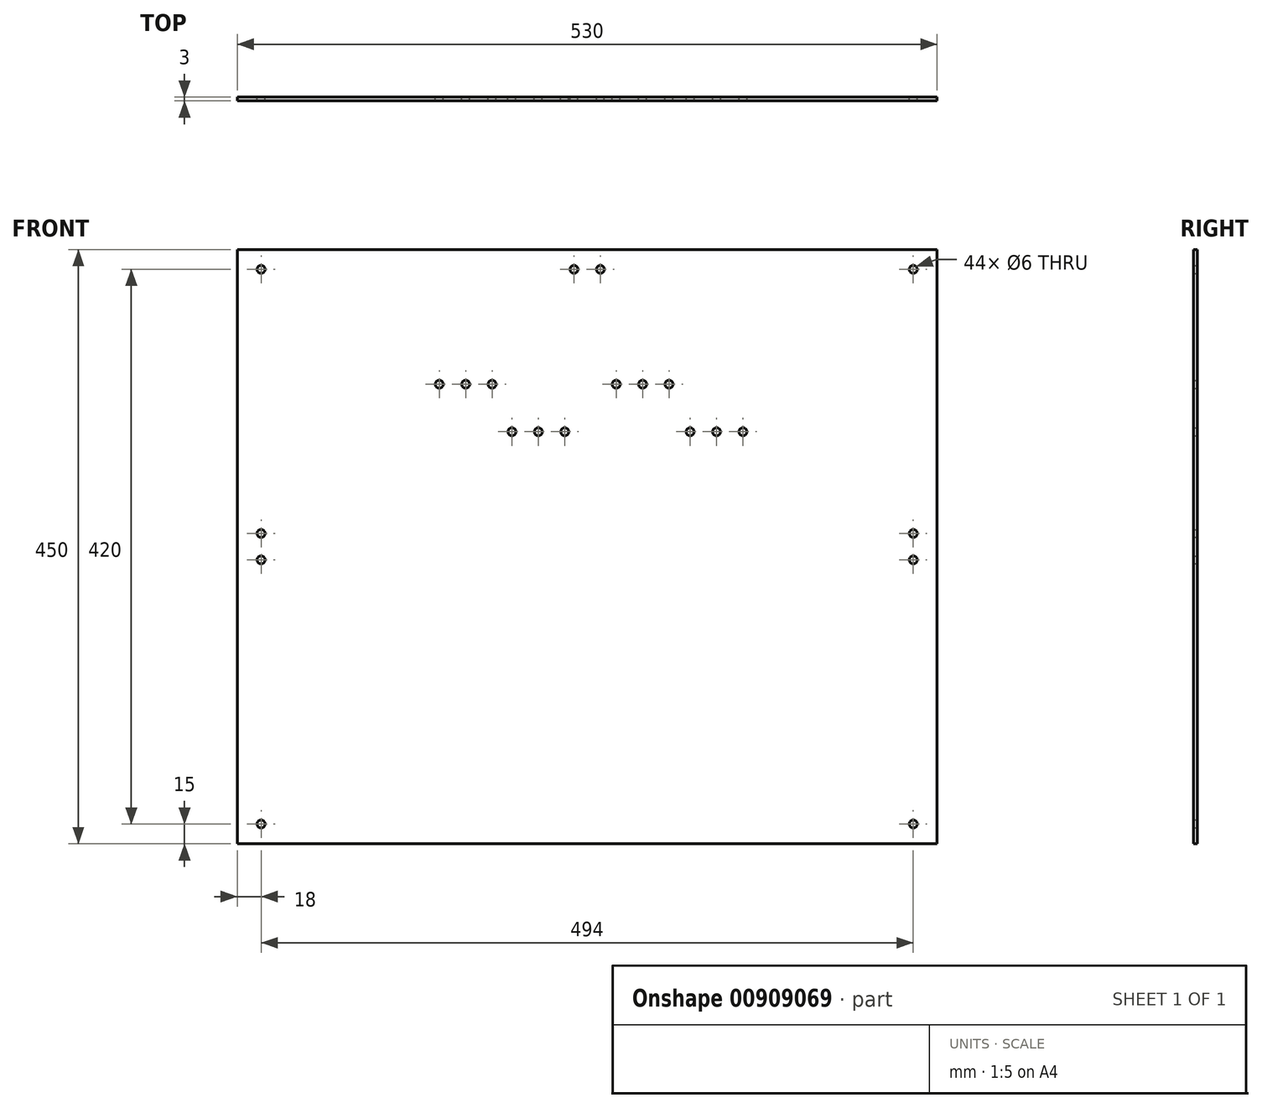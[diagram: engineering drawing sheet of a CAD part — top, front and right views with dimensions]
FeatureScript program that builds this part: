
annotation { "Feature Type Name" : "Feature", "Feature Type Description" : "" }
export const myFeature = defineFeature(function(context is Context, id is Id, definition is map)
    precondition{}
    {
        {
            var Q0;
            Q0=qCreatedBy(makeId("Front.planeOp"),FACE);
            var sketch = newSketch(context, id + "F0", { "sketchPlane" : qUnion([Q0])});
            skLineSegment(sketch, "E0.bottom", {"start": v(0, 0) * mm, "end": v(530, 0) * mm});
            skLineSegment(sketch, "E0.top", {"start": v(0, 450) * mm, "end": v(530, 450) * mm});
            skLineSegment(sketch, "E0.left", {"start": v(0, 0) * mm, "end": v(0, 450) * mm});
            skLineSegment(sketch, "E0.right", {"start": v(530, 0) * mm, "end": v(530, 450) * mm});
            skCircle(sketch, "E1", {"center": v(18, 15) * mm, "radius": 3 * mm});
            skCircle(sketch, "E2", {"center": v(512, 15) * mm, "radius": 3 * mm});
            skCircle(sketch, "E3", {"center": v(18, 435) * mm, "radius": 3 * mm});
            skCircle(sketch, "E4", {"center": v(512, 435) * mm, "radius": 3 * mm});
            skLineSegment(sketch, "E5.bottom", {"start": v(395, 80) * mm, "end": v(135, 80) * mm});
            skLineSegment(sketch, "E5.top", {"start": v(395, 330) * mm, "end": v(135, 330) * mm});
            skLineSegment(sketch, "E5.left", {"start": v(410, 95) * mm, "end": v(410, 315) * mm});
            skLineSegment(sketch, "E5.right", {"start": v(120, 95) * mm, "end": v(120, 315) * mm});
            skPoint(sketch, "E5.middle", {"position": v(265, 205) * mm});
            skPoint(sketch, "E6.visualSharp", {"position": v(120, 330) * mm});
            skArc(sketch, "E6.filletArc", {"start": v(135, 330) * mm, "mid": v(124.4, 325.6) * mm, "end": v(120, 315) * mm});
            skPoint(sketch, "E7.visualSharp", {"position": v(410, 330) * mm});
            skArc(sketch, "E7.filletArc", {"start": v(410, 315) * mm, "mid": v(405.6, 325.6) * mm, "end": v(395, 330) * mm});
            skPoint(sketch, "E8.visualSharp", {"position": v(120, 80) * mm});
            skArc(sketch, "E8.filletArc", {"start": v(120, 95) * mm, "mid": v(124.4, 84.4) * mm, "end": v(135, 80) * mm});
            skPoint(sketch, "E9.visualSharp", {"position": v(410, 80) * mm});
            skArc(sketch, "E9.filletArc", {"start": v(395, 80) * mm, "mid": v(405.6, 84.4) * mm, "end": v(410, 95) * mm});
            skCircle(sketch, "E10", {"center": v(153, 348) * mm, "radius": 3 * mm});
            skCircle(sketch, "E11", {"center": v(173, 348) * mm, "radius": 3 * mm});
            skCircle(sketch, "E12", {"center": v(193, 348) * mm, "radius": 3 * mm});
            skCircle(sketch, "E13", {"center": v(208, 312) * mm, "radius": 3 * mm});
            skCircle(sketch, "E14", {"center": v(228, 312) * mm, "radius": 3 * mm});
            skCircle(sketch, "E15", {"center": v(248, 312) * mm, "radius": 3 * mm});
            skCircle(sketch, "E16", {"center": v(287, 348) * mm, "radius": 3 * mm});
            skCircle(sketch, "E17", {"center": v(307, 348) * mm, "radius": 3 * mm});
            skCircle(sketch, "E18", {"center": v(327, 348) * mm, "radius": 3 * mm});
            skCircle(sketch, "E19", {"center": v(343, 312) * mm, "radius": 3 * mm});
            skCircle(sketch, "E20", {"center": v(363, 312) * mm, "radius": 3 * mm});
            skCircle(sketch, "E21", {"center": v(383, 312) * mm, "radius": 3 * mm});
            skCircle(sketch, "E22", {"center": v(18, 235) * mm, "radius": 3 * mm});
            skCircle(sketch, "E23", {"center": v(18, 215) * mm, "radius": 3 * mm});
            skCircle(sketch, "E24", {"center": v(512, 235) * mm, "radius": 3 * mm});
            skCircle(sketch, "E25", {"center": v(512, 215) * mm, "radius": 3 * mm});
            skCircle(sketch, "E26", {"center": v(255, 435) * mm, "radius": 3 * mm});
            skCircle(sketch, "E27", {"center": v(275, 435) * mm, "radius": 3 * mm});
            skSolve(sketch);
        }
        {
            var Q0;
            Q0=makeQuery(id+"F0.imprint","IMPRINT",FACE,{"disambiguationData":[TD([[makeQuery(id+"F0.imprint","IMPRINT",EDGE,{"derivedFrom":sQuery(id+"F0.wireOp",EDGE,"E0.bottom")}),1.0]])]});
            var Q1;
            Q1=makeQuery(id+"F0.imprint","IMPRINT",FACE,{"disambiguationData":[TD([[makeQuery(id+"F0.imprint","IMPRINT",EDGE,{"derivedFrom":sQuery(id+"F0.wireOp",EDGE,"E5.bottom")}),-1.0]])]});
            extrude(context, id + "F1", {"entities" : qUnion([Q0, Q1]), "depth" : 3 * mm, "offsetDistance" : 25 * mm});
        }
    });
